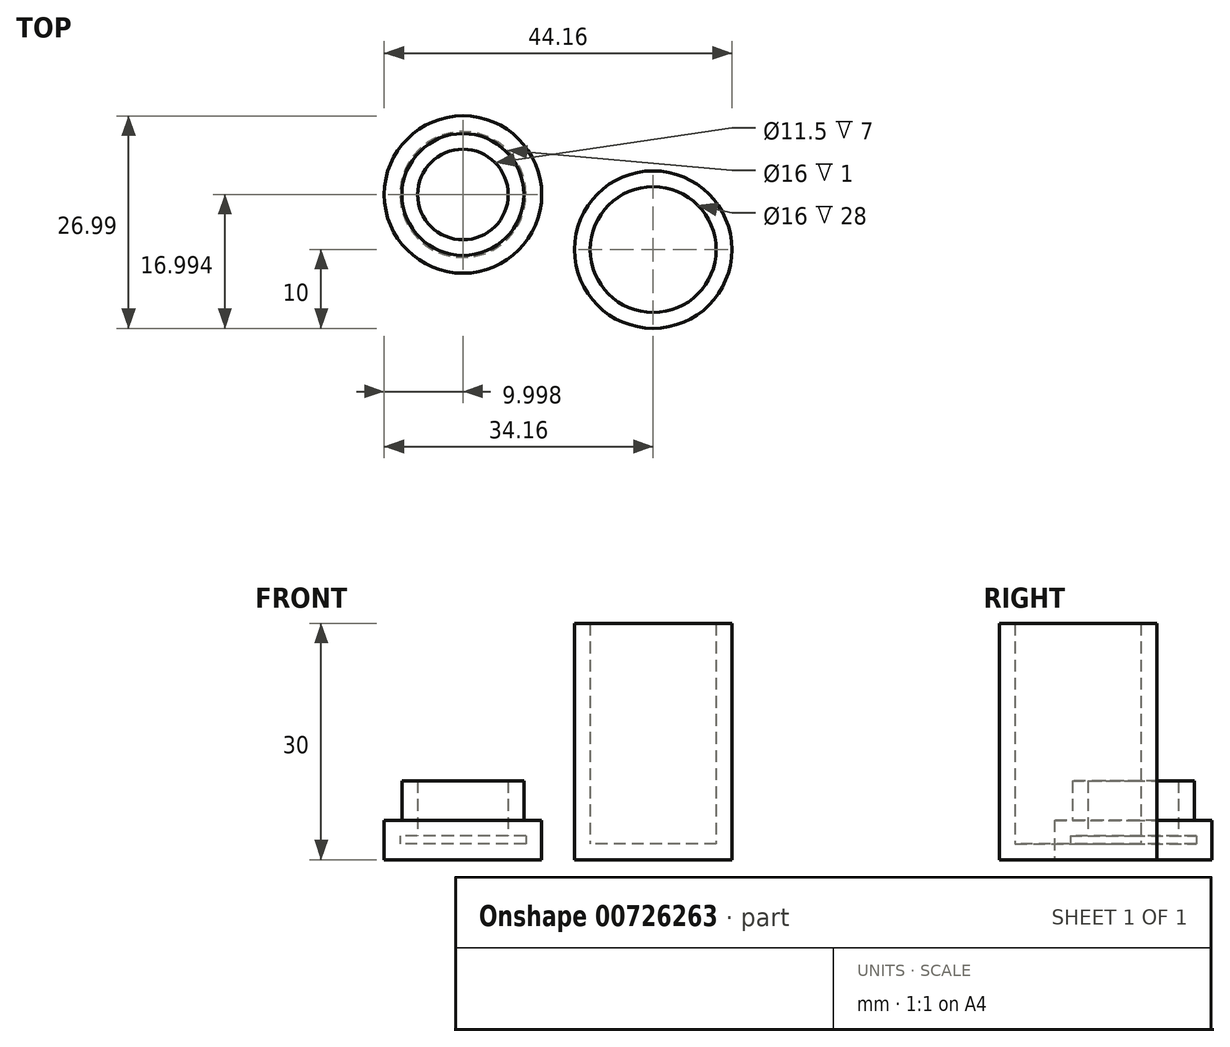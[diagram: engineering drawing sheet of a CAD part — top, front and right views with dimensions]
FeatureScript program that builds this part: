
annotation { "Feature Type Name" : "Feature", "Feature Type Description" : "" }
export const myFeature = defineFeature(function(context is Context, id is Id, definition is map)
    precondition{}
    {
        {
            var Q0;
            Q0=qCreatedBy(makeId("Top.planeOp"),FACE);
            var sketch = newSketch(context, id + "F0", { "sketchPlane" : qUnion([Q0])});
            skCircle(sketch, "E0", {"center": v(0, 0) * mm, "radius": 10 * mm});
            skSolve(sketch);
        }
        {
            var Q0;
            Q0 = qSketchRegion(id + "F0", true);
            extrude(context, id + "F1", {"entities" : qUnion([Q0]), "depth" : 30 * mm, "offsetDistance" : 25.4 * mm});
        }
        {
            var Q0;
            Q0=makeQuery(id+"F1.opExtrude","CAP_FACE",FACE,{"disambiguationData":[OSD([sQuery(id+"F0.wireOp",EDGE,"E0")])],"isStart":false});
            shell(context, id + "F2", {"entities" : qUnion([Q0]), "thickness" : 2 * mm});
        }
        {
            var Q0;
            Q0=qCreatedBy(makeId("Top.planeOp"),FACE);
            var sketch = newSketch(context, id + "F3", { "sketchPlane" : qUnion([Q0])});
            skCircle(sketch, "E1", {"center": v(-24.16, 7) * mm, "radius": 10 * mm});
            skCircle(sketch, "E2", {"center": v(-24.16, 7) * mm, "radius": 7.75 * mm});
            skSolve(sketch);
        }
        {
            var Q0;
            Q0=makeQuery(id+"F3.imprint","IMPRINT",FACE,{"disambiguationData":[TD([[makeQuery(id+"F3.imprint","IMPRINT",EDGE,{"derivedFrom":sQuery(id+"F3.wireOp",EDGE,"E2")}),1.0]])]});
            extrude(context, id + "F4", {"entities" : qUnion([Q0]), "depth" : 10 * mm, "offsetDistance" : 25 * mm});
        }
        {
            var Q0;
            Q0 = qSketchRegion(id + "F3", true);
            extrude(context, id + "F5", {"entities" : qUnion([Q0]), "operationType" : NewBodyOperationType.ADD, "depth" : 5 * mm, "offsetDistance" : 25 * mm});
        }
        {
            var Q0;
            Q0=makeQuery(id+"F4.opExtrude","CAP_FACE",FACE,{"disambiguationData":[OSD([sQuery(id+"F3.wireOp",EDGE,"E2")])],"isStart":false});
            shell(context, id + "F6", {"entities" : qUnion([Q0]), "thickness" : 2 * mm});
        }
    });
